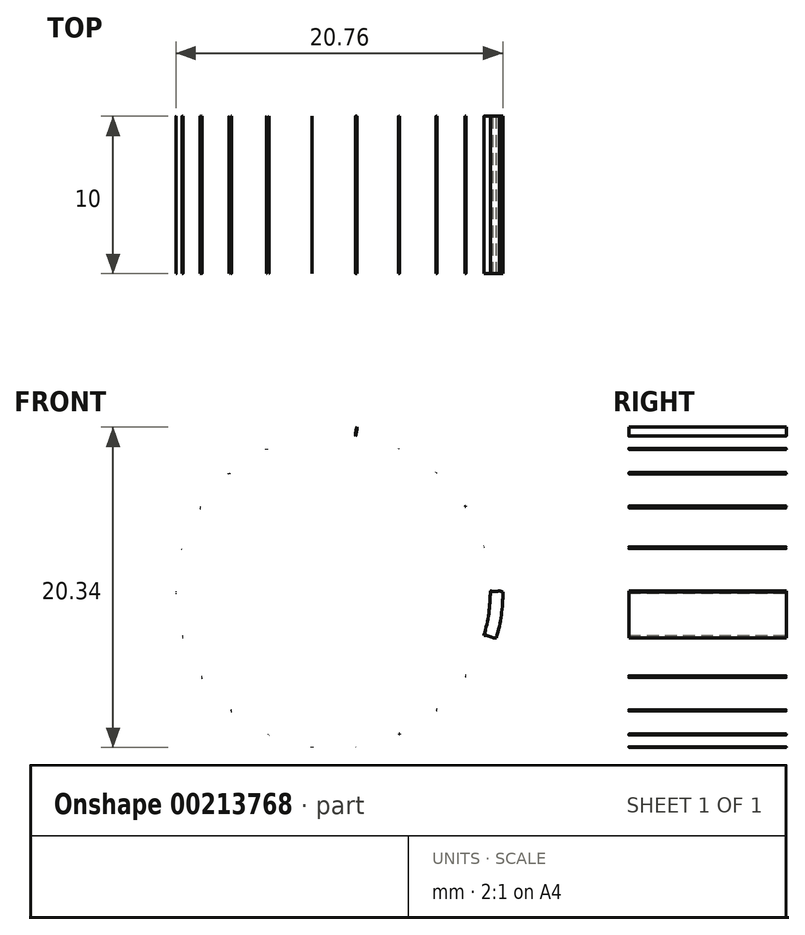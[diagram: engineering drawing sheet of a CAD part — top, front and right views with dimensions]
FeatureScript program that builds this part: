
annotation { "Feature Type Name" : "Feature", "Feature Type Description" : "" }
export const myFeature = defineFeature(function(context is Context, id is Id, definition is map)
    precondition{}
    {
        {
            var Q0;
            Q0=qCreatedBy(makeId("Front.planeOp"),FACE);
            var sketch = newSketch(context, id + "F0", { "sketchPlane" : qUnion([Q0])});
            skCircle(sketch, "E0", {"center": v(0, 0) * mm, "radius": 8.88 * mm, "construction": true});
            skCircle(sketch, "E1.0", {"center": v(0, 0) * mm, "radius": 11.88 * mm, "construction": true});
            skCircle(sketch, "E2.0", {"center": v(0, 0) * mm, "radius": 10.38 * mm, "construction": true});
            skCircle(sketch, "E3", {"center": v(0, 10.38) * mm, "radius": 1.5 * mm});
            skCircle(sketch, "E4.1.0", {"center": v(2.92, 9.96) * mm, "radius": 1.5 * mm});
            skCircle(sketch, "E4.2.0", {"center": v(5.6, 8.73) * mm, "radius": 1.5 * mm});
            skCircle(sketch, "E4.3.0", {"center": v(7.83, 6.8) * mm, "radius": 1.5 * mm});
            skCircle(sketch, "E4.4.0", {"center": v(9.43, 4.33) * mm, "radius": 1.5 * mm});
            skCircle(sketch, "E4.5.0", {"center": v(10.27, 1.5) * mm, "radius": 1.5 * mm});
            skCircle(sketch, "E4.6.0", {"center": v(10.27, -1.44) * mm, "radius": 1.5 * mm});
            skCircle(sketch, "E4.7.0", {"center": v(9.45, -4.27) * mm, "radius": 1.5 * mm});
            skCircle(sketch, "E4.8.0", {"center": v(7.87, -6.76) * mm, "radius": 1.5 * mm});
            skCircle(sketch, "E4.9.0", {"center": v(5.65, -8.7) * mm, "radius": 1.5 * mm});
            skCircle(sketch, "E4.10.0", {"center": v(2.98, -9.94) * mm, "radius": 1.5 * mm});
            skCircle(sketch, "E4.11.0", {"center": v(0.06, -10.37) * mm, "radius": 1.5 * mm});
            skCircle(sketch, "E4.12.0", {"center": v(-2.86, -9.97) * mm, "radius": 1.5 * mm});
            skCircle(sketch, "E4.13.0", {"center": v(-5.55, -8.77) * mm, "radius": 1.5 * mm});
            skCircle(sketch, "E4.14.0", {"center": v(-7.8, -6.85) * mm, "radius": 1.5 * mm});
            skCircle(sketch, "E4.15.0", {"center": v(-9.4, -4.38) * mm, "radius": 1.5 * mm});
            skCircle(sketch, "E4.16.0", {"center": v(-10.26, -1.56) * mm, "radius": 1.5 * mm});
            skCircle(sketch, "E4.17.0", {"center": v(-10.28, 1.38) * mm, "radius": 1.5 * mm});
            skCircle(sketch, "E4.18.0", {"center": v(-9.48, 4.22) * mm, "radius": 1.5 * mm});
            skCircle(sketch, "E4.19.0", {"center": v(-7.9, 6.72) * mm, "radius": 1.5 * mm});
            skCircle(sketch, "E4.20.0", {"center": v(-5.7, 8.67) * mm, "radius": 1.5 * mm});
            skCircle(sketch, "E4.21.0", {"center": v(-3.03, 9.92) * mm, "radius": 1.5 * mm});
            skLineSegment(sketch, "E4.anchor1", {"start": v(0, 0) * mm, "end": v(0, 10.38) * mm, "construction": true});
            skLineSegment(sketch, "E4.anchor2", {"start": v(0, 0) * mm, "end": v(-3.03, 9.92) * mm, "construction": true});
            skCircle(sketch, "E5.0", {"center": v(0, 0) * mm, "radius": 10.78 * mm});
            skCircle(sketch, "E6.0", {"center": v(0, 0) * mm, "radius": 9.98 * mm});
            skSolve(sketch);
        }
        {
            var Q0;
            {var subQ0=sQuery(id+"F0.wireOp",EDGE,"E4.1.0");var subQ1=sQuery(id+"F0.wireOp",EDGE,"E3");var subQ2=makeQuery(id+"F0.imprint","INTERSECT",VERTEX,{"disambiguationData":[OD(0.0)],"derivedFrom":[subQ1,subQ0]});Q0=makeQuery(id+"F0.imprint","IMPRINT",FACE,{"disambiguationData":[TD([[makeQuery(id+"F0.imprint","IMPRINT",EDGE,{"disambiguationData":[TD([[subQ2,-1.0]])],"derivedFrom":subQ1}),1.0]])]});}
            var Q1;
            {var subQ0=sQuery(id+"F0.wireOp",EDGE,"E4.1.0");var subQ1=sQuery(id+"F0.wireOp",EDGE,"E3");var subQ2=makeQuery(id+"F0.imprint","INTERSECT",VERTEX,{"disambiguationData":[OD(0.0)],"derivedFrom":[subQ1,subQ0]});Q1=makeQuery(id+"F0.imprint","IMPRINT",FACE,{"disambiguationData":[TD([[makeQuery(id+"F0.imprint","IMPRINT",EDGE,{"disambiguationData":[TD([[subQ2,1.0]])],"derivedFrom":subQ1}),-1.0]])]});}
            var Q2;
            {var subQ0=sQuery(id+"F0.wireOp",EDGE,"E4.2.0");var subQ1=sQuery(id+"F0.wireOp",EDGE,"E4.1.0");var subQ2=makeQuery(id+"F0.imprint","INTERSECT",VERTEX,{"disambiguationData":[OD(0.0)],"derivedFrom":[subQ1,subQ0]});Q2=makeQuery(id+"F0.imprint","IMPRINT",FACE,{"disambiguationData":[TD([[makeQuery(id+"F0.imprint","IMPRINT",EDGE,{"disambiguationData":[TD([[subQ2,1.0]])],"derivedFrom":subQ1}),-1.0]])]});}
            var Q3;
            {var subQ0=sQuery(id+"F0.wireOp",EDGE,"E4.3.0");var subQ1=sQuery(id+"F0.wireOp",EDGE,"E4.2.0");var subQ2=makeQuery(id+"F0.imprint","INTERSECT",VERTEX,{"disambiguationData":[OD(0.0)],"derivedFrom":[subQ1,subQ0]});Q3=makeQuery(id+"F0.imprint","IMPRINT",FACE,{"disambiguationData":[TD([[makeQuery(id+"F0.imprint","IMPRINT",EDGE,{"disambiguationData":[TD([[subQ2,1.0]])],"derivedFrom":subQ1}),-1.0]])]});}
            var Q4;
            {var subQ0=sQuery(id+"F0.wireOp",EDGE,"E4.4.0");var subQ1=sQuery(id+"F0.wireOp",EDGE,"E4.3.0");var subQ2=makeQuery(id+"F0.imprint","INTERSECT",VERTEX,{"disambiguationData":[OD(0.0)],"derivedFrom":[subQ1,subQ0]});Q4=makeQuery(id+"F0.imprint","IMPRINT",FACE,{"disambiguationData":[TD([[makeQuery(id+"F0.imprint","IMPRINT",EDGE,{"disambiguationData":[TD([[subQ2,1.0]])],"derivedFrom":subQ1}),-1.0]])]});}
            var Q5;
            {var subQ0=sQuery(id+"F0.wireOp",EDGE,"E4.5.0");var subQ1=sQuery(id+"F0.wireOp",EDGE,"E4.4.0");var subQ2=makeQuery(id+"F0.imprint","INTERSECT",VERTEX,{"disambiguationData":[OD(0.0)],"derivedFrom":[subQ1,subQ0]});Q5=makeQuery(id+"F0.imprint","IMPRINT",FACE,{"disambiguationData":[TD([[makeQuery(id+"F0.imprint","IMPRINT",EDGE,{"disambiguationData":[TD([[subQ2,1.0]])],"derivedFrom":subQ1}),-1.0]])]});}
            var Q6;
            {var subQ0=sQuery(id+"F0.wireOp",EDGE,"E4.6.0");var subQ1=sQuery(id+"F0.wireOp",EDGE,"E4.5.0");var subQ2=makeQuery(id+"F0.imprint","INTERSECT",VERTEX,{"disambiguationData":[OD(0.0)],"derivedFrom":[subQ1,subQ0]});Q6=makeQuery(id+"F0.imprint","IMPRINT",FACE,{"disambiguationData":[TD([[makeQuery(id+"F0.imprint","IMPRINT",EDGE,{"disambiguationData":[TD([[subQ2,1.0]])],"derivedFrom":subQ1}),-1.0]])]});}
            var Q7;
            {var subQ0=sQuery(id+"F0.wireOp",EDGE,"E4.7.0");var subQ1=sQuery(id+"F0.wireOp",EDGE,"E4.6.0");var subQ2=makeQuery(id+"F0.imprint","INTERSECT",VERTEX,{"disambiguationData":[OD(0.0)],"derivedFrom":[subQ1,subQ0]});Q7=makeQuery(id+"F0.imprint","IMPRINT",FACE,{"disambiguationData":[TD([[makeQuery(id+"F0.imprint","IMPRINT",EDGE,{"disambiguationData":[TD([[subQ2,1.0]])],"derivedFrom":subQ1}),-1.0]])]});}
            var Q8;
            {var subQ0=sQuery(id+"F0.wireOp",EDGE,"E4.8.0");var subQ1=sQuery(id+"F0.wireOp",EDGE,"E4.7.0");var subQ2=makeQuery(id+"F0.imprint","INTERSECT",VERTEX,{"disambiguationData":[OD(0.0)],"derivedFrom":[subQ1,subQ0]});Q8=makeQuery(id+"F0.imprint","IMPRINT",FACE,{"disambiguationData":[TD([[makeQuery(id+"F0.imprint","IMPRINT",EDGE,{"disambiguationData":[TD([[subQ2,1.0]])],"derivedFrom":subQ1}),-1.0]])]});}
            var Q9;
            {var subQ0=sQuery(id+"F0.wireOp",EDGE,"E4.9.0");var subQ1=sQuery(id+"F0.wireOp",EDGE,"E4.8.0");var subQ2=makeQuery(id+"F0.imprint","INTERSECT",VERTEX,{"disambiguationData":[OD(0.0)],"derivedFrom":[subQ1,subQ0]});Q9=makeQuery(id+"F0.imprint","IMPRINT",FACE,{"disambiguationData":[TD([[makeQuery(id+"F0.imprint","IMPRINT",EDGE,{"disambiguationData":[TD([[subQ2,1.0]])],"derivedFrom":subQ1}),-1.0]])]});}
            var Q10;
            {var subQ0=sQuery(id+"F0.wireOp",EDGE,"E4.10.0");var subQ1=sQuery(id+"F0.wireOp",EDGE,"E4.9.0");var subQ2=makeQuery(id+"F0.imprint","INTERSECT",VERTEX,{"disambiguationData":[OD(0.0)],"derivedFrom":[subQ1,subQ0]});Q10=makeQuery(id+"F0.imprint","IMPRINT",FACE,{"disambiguationData":[TD([[makeQuery(id+"F0.imprint","IMPRINT",EDGE,{"disambiguationData":[TD([[subQ2,1.0]])],"derivedFrom":subQ1}),-1.0]])]});}
            var Q11;
            {var subQ0=sQuery(id+"F0.wireOp",EDGE,"E4.11.0");var subQ1=sQuery(id+"F0.wireOp",EDGE,"E4.10.0");var subQ2=makeQuery(id+"F0.imprint","INTERSECT",VERTEX,{"disambiguationData":[OD(0.0)],"derivedFrom":[subQ1,subQ0]});Q11=makeQuery(id+"F0.imprint","IMPRINT",FACE,{"disambiguationData":[TD([[makeQuery(id+"F0.imprint","IMPRINT",EDGE,{"disambiguationData":[TD([[subQ2,1.0]])],"derivedFrom":subQ1}),-1.0]])]});}
            var Q12;
            {var subQ0=sQuery(id+"F0.wireOp",EDGE,"E4.12.0");var subQ1=sQuery(id+"F0.wireOp",EDGE,"E4.11.0");var subQ2=makeQuery(id+"F0.imprint","INTERSECT",VERTEX,{"disambiguationData":[OD(0.0)],"derivedFrom":[subQ1,subQ0]});Q12=makeQuery(id+"F0.imprint","IMPRINT",FACE,{"disambiguationData":[TD([[makeQuery(id+"F0.imprint","IMPRINT",EDGE,{"disambiguationData":[TD([[subQ2,1.0]])],"derivedFrom":subQ1}),-1.0]])]});}
            var Q13;
            {var subQ0=sQuery(id+"F0.wireOp",EDGE,"E4.13.0");var subQ1=sQuery(id+"F0.wireOp",EDGE,"E4.12.0");var subQ2=makeQuery(id+"F0.imprint","INTERSECT",VERTEX,{"disambiguationData":[OD(0.0)],"derivedFrom":[subQ1,subQ0]});Q13=makeQuery(id+"F0.imprint","IMPRINT",FACE,{"disambiguationData":[TD([[makeQuery(id+"F0.imprint","IMPRINT",EDGE,{"disambiguationData":[TD([[subQ2,1.0]])],"derivedFrom":subQ1}),-1.0]])]});}
            var Q14;
            {var subQ0=sQuery(id+"F0.wireOp",EDGE,"E4.14.0");var subQ1=sQuery(id+"F0.wireOp",EDGE,"E4.13.0");var subQ2=makeQuery(id+"F0.imprint","INTERSECT",VERTEX,{"disambiguationData":[OD(0.0)],"derivedFrom":[subQ1,subQ0]});Q14=makeQuery(id+"F0.imprint","IMPRINT",FACE,{"disambiguationData":[TD([[makeQuery(id+"F0.imprint","IMPRINT",EDGE,{"disambiguationData":[TD([[subQ2,1.0]])],"derivedFrom":subQ1}),-1.0]])]});}
            var Q15;
            {var subQ0=sQuery(id+"F0.wireOp",EDGE,"E4.15.0");var subQ1=sQuery(id+"F0.wireOp",EDGE,"E4.14.0");var subQ2=makeQuery(id+"F0.imprint","INTERSECT",VERTEX,{"disambiguationData":[OD(0.0)],"derivedFrom":[subQ1,subQ0]});Q15=makeQuery(id+"F0.imprint","IMPRINT",FACE,{"disambiguationData":[TD([[makeQuery(id+"F0.imprint","IMPRINT",EDGE,{"disambiguationData":[TD([[subQ2,1.0]])],"derivedFrom":subQ1}),-1.0]])]});}
            var Q16;
            {var subQ0=sQuery(id+"F0.wireOp",EDGE,"E4.16.0");var subQ1=sQuery(id+"F0.wireOp",EDGE,"E4.15.0");var subQ2=makeQuery(id+"F0.imprint","INTERSECT",VERTEX,{"disambiguationData":[OD(0.0)],"derivedFrom":[subQ1,subQ0]});Q16=makeQuery(id+"F0.imprint","IMPRINT",FACE,{"disambiguationData":[TD([[makeQuery(id+"F0.imprint","IMPRINT",EDGE,{"disambiguationData":[TD([[subQ2,1.0]])],"derivedFrom":subQ1}),-1.0]])]});}
            var Q17;
            {var subQ0=sQuery(id+"F0.wireOp",EDGE,"E4.17.0");var subQ1=sQuery(id+"F0.wireOp",EDGE,"E4.16.0");var subQ2=makeQuery(id+"F0.imprint","INTERSECT",VERTEX,{"disambiguationData":[OD(0.0)],"derivedFrom":[subQ1,subQ0]});Q17=makeQuery(id+"F0.imprint","IMPRINT",FACE,{"disambiguationData":[TD([[makeQuery(id+"F0.imprint","IMPRINT",EDGE,{"disambiguationData":[TD([[subQ2,1.0]])],"derivedFrom":subQ1}),-1.0]])]});}
            var Q18;
            {var subQ0=sQuery(id+"F0.wireOp",EDGE,"E4.18.0");var subQ1=sQuery(id+"F0.wireOp",EDGE,"E4.17.0");var subQ2=makeQuery(id+"F0.imprint","INTERSECT",VERTEX,{"disambiguationData":[OD(0.0)],"derivedFrom":[subQ1,subQ0]});Q18=makeQuery(id+"F0.imprint","IMPRINT",FACE,{"disambiguationData":[TD([[makeQuery(id+"F0.imprint","IMPRINT",EDGE,{"disambiguationData":[TD([[subQ2,1.0]])],"derivedFrom":subQ1}),-1.0]])]});}
            var Q19;
            {var subQ0=sQuery(id+"F0.wireOp",EDGE,"E4.19.0");var subQ1=sQuery(id+"F0.wireOp",EDGE,"E4.18.0");var subQ2=makeQuery(id+"F0.imprint","INTERSECT",VERTEX,{"disambiguationData":[OD(0.0)],"derivedFrom":[subQ1,subQ0]});Q19=makeQuery(id+"F0.imprint","IMPRINT",FACE,{"disambiguationData":[TD([[makeQuery(id+"F0.imprint","IMPRINT",EDGE,{"disambiguationData":[TD([[subQ2,1.0]])],"derivedFrom":subQ1}),-1.0]])]});}
            var Q20;
            {var subQ0=sQuery(id+"F0.wireOp",EDGE,"E4.20.0");var subQ1=sQuery(id+"F0.wireOp",EDGE,"E4.19.0");var subQ2=makeQuery(id+"F0.imprint","INTERSECT",VERTEX,{"disambiguationData":[OD(0.0)],"derivedFrom":[subQ1,subQ0]});Q20=makeQuery(id+"F0.imprint","IMPRINT",FACE,{"disambiguationData":[TD([[makeQuery(id+"F0.imprint","IMPRINT",EDGE,{"disambiguationData":[TD([[subQ2,1.0]])],"derivedFrom":subQ1}),-1.0]])]});}
            var Q21;
            {var subQ0=sQuery(id+"F0.wireOp",EDGE,"E4.21.0");var subQ1=sQuery(id+"F0.wireOp",EDGE,"E4.20.0");var subQ2=makeQuery(id+"F0.imprint","INTERSECT",VERTEX,{"disambiguationData":[OD(0.0)],"derivedFrom":[subQ1,subQ0]});Q21=makeQuery(id+"F0.imprint","IMPRINT",FACE,{"disambiguationData":[TD([[makeQuery(id+"F0.imprint","IMPRINT",EDGE,{"disambiguationData":[TD([[subQ2,1.0]])],"derivedFrom":subQ1}),-1.0]])]});}
            extrude(context, id + "F1", {"entities" : qUnion([Q0, Q1, Q2, Q3, Q4, Q5, Q6, Q7, Q8, Q9, Q10, Q11, Q12, Q13, Q14, Q15, Q16, Q17, Q18, Q19, Q20, Q21]), "depth" : 5 * mm, "hasSecondDirection" : true, "secondDirectionOppositeDirection" : true, "secondDirectionDepth" : 5 * mm});
        }
    });
